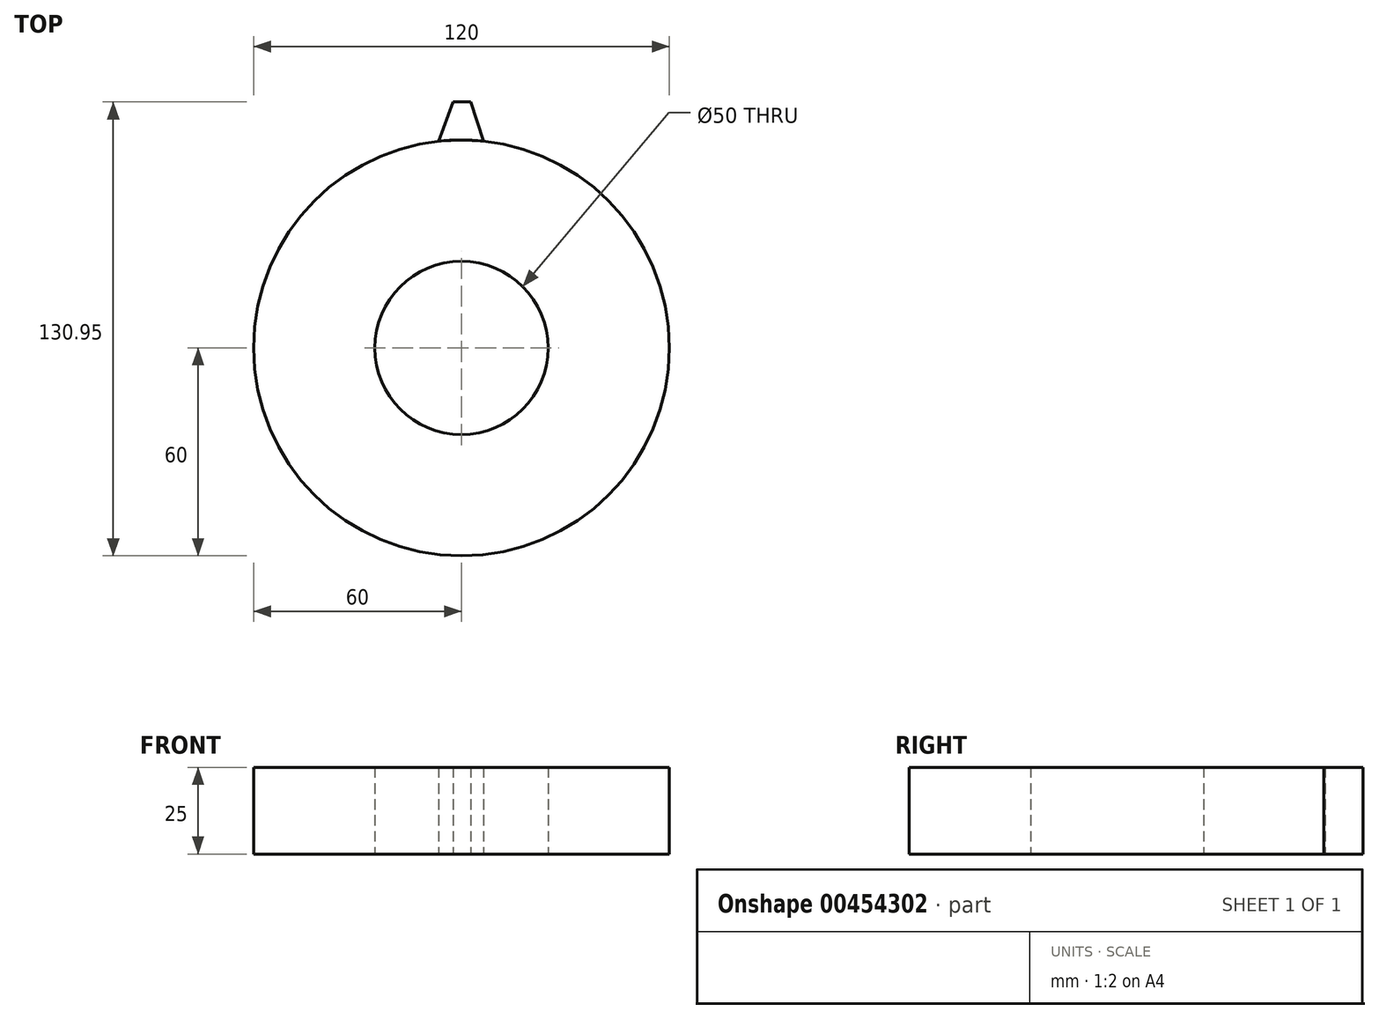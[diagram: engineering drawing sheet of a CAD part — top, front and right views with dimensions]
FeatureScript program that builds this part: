
annotation { "Feature Type Name" : "Feature", "Feature Type Description" : "" }
export const myFeature = defineFeature(function(context is Context, id is Id, definition is map)
    precondition{}
    {
        {
            var Q0;
            Q0=qCreatedBy(makeId("Top.planeOp"),FACE);
            var sketch = newSketch(context, id + "F0", { "sketchPlane" : qUnion([Q0])});
            skCircle(sketch, "E0", {"center": v(0, 0) * mm, "radius": 60 * mm});
            skSolve(sketch);
        }
        {
            var Q0;
            Q0=qCreatedBy(makeId("Top.planeOp"),FACE);
            var sketch = newSketch(context, id + "F1", { "sketchPlane" : qUnion([Q0])});
            skCircle(sketch, "E1", {"center": v(0, 0) * mm, "radius": 25 * mm});
            skSolve(sketch);
        }
        {
            var Q0;
            Q0=qCreatedBy(makeId("Top.planeOp"),FACE);
            var sketch = newSketch(context, id + "F2", { "sketchPlane" : qUnion([Q0])});
            skLineSegment(sketch, "E2", {"start": v(-6.64, 59.63) * mm, "end": v(-2.43, 70.95) * mm});
            skLineSegment(sketch, "E3", {"start": v(-2.43, 70.95) * mm, "end": v(2.67, 70.95) * mm});
            skLineSegment(sketch, "E4", {"start": v(2.67, 70.95) * mm, "end": v(6.3, 59.67) * mm});
            skArc(sketch, "E5", {"start": v(-6.64, 59.63) * mm, "mid": v(-0.17, 60) * mm, "end": v(6.3, 59.67) * mm});
            skSolve(sketch);
        }
        {
            var Q0;
            Q0=qCreatedBy(makeId("Top.planeOp"),FACE);
            var sketch = newSketch(context, id + "F3", { "sketchPlane" : qUnion([Q0])});
            skCircle(sketch, "E6", {"center": v(0, 0) * mm, "radius": 60 * mm});
            skSolve(sketch);
        }
        {
            var Q0;
            Q0 = qSketchRegion(id + "F3", true);
            var Q1;
            Q1 = qSketchRegion(id + "F2", true);
            var Q2;
            Q2=makeQuery(id+"FFwbZkJwYjuvKQh_0.25.F2.imprint","IMPRINT",FACE,{"disambiguationData":[TD([[makeQuery(id+"FFwbZkJwYjuvKQh_0.25.F2.imprint","IMPRINT",EDGE,{"derivedFrom":sQuery(id+"FFwbZkJwYjuvKQh_0.25.F2.wireOp",EDGE,"E2")}),-1.0]])]});
            var Q3;
            Q3=makeQuery(id+"FFwbZkJwYjuvKQh_0.24.F2.imprint","IMPRINT",FACE,{"disambiguationData":[TD([[makeQuery(id+"FFwbZkJwYjuvKQh_0.24.F2.imprint","IMPRINT",EDGE,{"derivedFrom":sQuery(id+"FFwbZkJwYjuvKQh_0.24.F2.wireOp",EDGE,"E2")}),-1.0]])]});
            var Q4;
            Q4=makeQuery(id+"FFwbZkJwYjuvKQh_0.23.F2.imprint","IMPRINT",FACE,{"disambiguationData":[TD([[makeQuery(id+"FFwbZkJwYjuvKQh_0.23.F2.imprint","IMPRINT",EDGE,{"derivedFrom":sQuery(id+"FFwbZkJwYjuvKQh_0.23.F2.wireOp",EDGE,"E2")}),-1.0]])]});
            var Q5;
            Q5=makeQuery(id+"FFwbZkJwYjuvKQh_0.22.F2.imprint","IMPRINT",FACE,{"disambiguationData":[TD([[makeQuery(id+"FFwbZkJwYjuvKQh_0.22.F2.imprint","IMPRINT",EDGE,{"derivedFrom":sQuery(id+"FFwbZkJwYjuvKQh_0.22.F2.wireOp",EDGE,"E2")}),-1.0]])]});
            var Q6;
            Q6=makeQuery(id+"FFwbZkJwYjuvKQh_0.21.F2.imprint","IMPRINT",FACE,{"disambiguationData":[TD([[makeQuery(id+"FFwbZkJwYjuvKQh_0.21.F2.imprint","IMPRINT",EDGE,{"derivedFrom":sQuery(id+"FFwbZkJwYjuvKQh_0.21.F2.wireOp",EDGE,"E2")}),-1.0]])]});
            var Q7;
            Q7=makeQuery(id+"FFwbZkJwYjuvKQh_0.20.F2.imprint","IMPRINT",FACE,{"disambiguationData":[TD([[makeQuery(id+"FFwbZkJwYjuvKQh_0.20.F2.imprint","IMPRINT",EDGE,{"derivedFrom":sQuery(id+"FFwbZkJwYjuvKQh_0.20.F2.wireOp",EDGE,"E2")}),-1.0]])]});
            var Q8;
            Q8=makeQuery(id+"FFwbZkJwYjuvKQh_0.19.F2.imprint","IMPRINT",FACE,{"disambiguationData":[TD([[makeQuery(id+"FFwbZkJwYjuvKQh_0.19.F2.imprint","IMPRINT",EDGE,{"derivedFrom":sQuery(id+"FFwbZkJwYjuvKQh_0.19.F2.wireOp",EDGE,"E2")}),-1.0]])]});
            var Q9;
            Q9=makeQuery(id+"FFwbZkJwYjuvKQh_0.18.F2.imprint","IMPRINT",FACE,{"disambiguationData":[TD([[makeQuery(id+"FFwbZkJwYjuvKQh_0.18.F2.imprint","IMPRINT",EDGE,{"derivedFrom":sQuery(id+"FFwbZkJwYjuvKQh_0.18.F2.wireOp",EDGE,"E2")}),-1.0]])]});
            var Q10;
            Q10=makeQuery(id+"FFwbZkJwYjuvKQh_0.17.F2.imprint","IMPRINT",FACE,{"disambiguationData":[TD([[makeQuery(id+"FFwbZkJwYjuvKQh_0.17.F2.imprint","IMPRINT",EDGE,{"derivedFrom":sQuery(id+"FFwbZkJwYjuvKQh_0.17.F2.wireOp",EDGE,"E2")}),-1.0]])]});
            var Q11;
            Q11=makeQuery(id+"FFwbZkJwYjuvKQh_0.16.F2.imprint","IMPRINT",FACE,{"disambiguationData":[TD([[makeQuery(id+"FFwbZkJwYjuvKQh_0.16.F2.imprint","IMPRINT",EDGE,{"derivedFrom":sQuery(id+"FFwbZkJwYjuvKQh_0.16.F2.wireOp",EDGE,"E2")}),-1.0]])]});
            var Q12;
            Q12=makeQuery(id+"FFwbZkJwYjuvKQh_0.15.F2.imprint","IMPRINT",FACE,{"disambiguationData":[TD([[makeQuery(id+"FFwbZkJwYjuvKQh_0.15.F2.imprint","IMPRINT",EDGE,{"derivedFrom":sQuery(id+"FFwbZkJwYjuvKQh_0.15.F2.wireOp",EDGE,"E2")}),-1.0]])]});
            var Q13;
            Q13=makeQuery(id+"FFwbZkJwYjuvKQh_0.14.F2.imprint","IMPRINT",FACE,{"disambiguationData":[TD([[makeQuery(id+"FFwbZkJwYjuvKQh_0.14.F2.imprint","IMPRINT",EDGE,{"derivedFrom":sQuery(id+"FFwbZkJwYjuvKQh_0.14.F2.wireOp",EDGE,"E2")}),-1.0]])]});
            var Q14;
            Q14=makeQuery(id+"FFwbZkJwYjuvKQh_0.13.F2.imprint","IMPRINT",FACE,{"disambiguationData":[TD([[makeQuery(id+"FFwbZkJwYjuvKQh_0.13.F2.imprint","IMPRINT",EDGE,{"derivedFrom":sQuery(id+"FFwbZkJwYjuvKQh_0.13.F2.wireOp",EDGE,"E2")}),-1.0]])]});
            var Q15;
            Q15=makeQuery(id+"FFwbZkJwYjuvKQh_0.12.F2.imprint","IMPRINT",FACE,{"disambiguationData":[TD([[makeQuery(id+"FFwbZkJwYjuvKQh_0.12.F2.imprint","IMPRINT",EDGE,{"derivedFrom":sQuery(id+"FFwbZkJwYjuvKQh_0.12.F2.wireOp",EDGE,"E2")}),-1.0]])]});
            var Q16;
            Q16=makeQuery(id+"FFwbZkJwYjuvKQh_0.11.F2.imprint","IMPRINT",FACE,{"disambiguationData":[TD([[makeQuery(id+"FFwbZkJwYjuvKQh_0.11.F2.imprint","IMPRINT",EDGE,{"derivedFrom":sQuery(id+"FFwbZkJwYjuvKQh_0.11.F2.wireOp",EDGE,"E2")}),-1.0]])]});
            var Q17;
            Q17=makeQuery(id+"FFwbZkJwYjuvKQh_0.10.F2.imprint","IMPRINT",FACE,{"disambiguationData":[TD([[makeQuery(id+"FFwbZkJwYjuvKQh_0.10.F2.imprint","IMPRINT",EDGE,{"derivedFrom":sQuery(id+"FFwbZkJwYjuvKQh_0.10.F2.wireOp",EDGE,"E2")}),-1.0]])]});
            var Q18;
            Q18=makeQuery(id+"FFwbZkJwYjuvKQh_0.9.F2.imprint","IMPRINT",FACE,{"disambiguationData":[TD([[makeQuery(id+"FFwbZkJwYjuvKQh_0.9.F2.imprint","IMPRINT",EDGE,{"derivedFrom":sQuery(id+"FFwbZkJwYjuvKQh_0.9.F2.wireOp",EDGE,"E2")}),-1.0]])]});
            var Q19;
            Q19=makeQuery(id+"FFwbZkJwYjuvKQh_0.8.F2.imprint","IMPRINT",FACE,{"disambiguationData":[TD([[makeQuery(id+"FFwbZkJwYjuvKQh_0.8.F2.imprint","IMPRINT",EDGE,{"derivedFrom":sQuery(id+"FFwbZkJwYjuvKQh_0.8.F2.wireOp",EDGE,"E2")}),-1.0]])]});
            var Q20;
            Q20=makeQuery(id+"FFwbZkJwYjuvKQh_0.7.F2.imprint","IMPRINT",FACE,{"disambiguationData":[TD([[makeQuery(id+"FFwbZkJwYjuvKQh_0.7.F2.imprint","IMPRINT",EDGE,{"derivedFrom":sQuery(id+"FFwbZkJwYjuvKQh_0.7.F2.wireOp",EDGE,"E2")}),-1.0]])]});
            var Q21;
            Q21=makeQuery(id+"FFwbZkJwYjuvKQh_0.6.F2.imprint","IMPRINT",FACE,{"disambiguationData":[TD([[makeQuery(id+"FFwbZkJwYjuvKQh_0.6.F2.imprint","IMPRINT",EDGE,{"derivedFrom":sQuery(id+"FFwbZkJwYjuvKQh_0.6.F2.wireOp",EDGE,"E2")}),-1.0]])]});
            var Q22;
            Q22=makeQuery(id+"FFwbZkJwYjuvKQh_0.5.F2.imprint","IMPRINT",FACE,{"disambiguationData":[TD([[makeQuery(id+"FFwbZkJwYjuvKQh_0.5.F2.imprint","IMPRINT",EDGE,{"derivedFrom":sQuery(id+"FFwbZkJwYjuvKQh_0.5.F2.wireOp",EDGE,"E2")}),-1.0]])]});
            var Q23;
            Q23=makeQuery(id+"FFwbZkJwYjuvKQh_0.4.F2.imprint","IMPRINT",FACE,{"disambiguationData":[TD([[makeQuery(id+"FFwbZkJwYjuvKQh_0.4.F2.imprint","IMPRINT",EDGE,{"derivedFrom":sQuery(id+"FFwbZkJwYjuvKQh_0.4.F2.wireOp",EDGE,"E2")}),-1.0]])]});
            var Q24;
            Q24=makeQuery(id+"FFwbZkJwYjuvKQh_0.3.F2.imprint","IMPRINT",FACE,{"disambiguationData":[TD([[makeQuery(id+"FFwbZkJwYjuvKQh_0.3.F2.imprint","IMPRINT",EDGE,{"derivedFrom":sQuery(id+"FFwbZkJwYjuvKQh_0.3.F2.wireOp",EDGE,"E2")}),-1.0]])]});
            var Q25;
            Q25=makeQuery(id+"FFwbZkJwYjuvKQh_0.2.F2.imprint","IMPRINT",FACE,{"disambiguationData":[TD([[makeQuery(id+"FFwbZkJwYjuvKQh_0.2.F2.imprint","IMPRINT",EDGE,{"derivedFrom":sQuery(id+"FFwbZkJwYjuvKQh_0.2.F2.wireOp",EDGE,"E2")}),-1.0]])]});
            var Q26;
            Q26=makeQuery(id+"FFwbZkJwYjuvKQh_0.1.F2.imprint","IMPRINT",FACE,{"disambiguationData":[TD([[makeQuery(id+"FFwbZkJwYjuvKQh_0.1.F2.imprint","IMPRINT",EDGE,{"derivedFrom":sQuery(id+"FFwbZkJwYjuvKQh_0.1.F2.wireOp",EDGE,"E2")}),-1.0]])]});
            extrude(context, id + "F4", {"entities" : qUnion([Q0, Q1, Q2, Q3, Q4, Q5, Q6, Q7, Q8, Q9, Q10, Q11, Q12, Q13, Q14, Q15, Q16, Q17, Q18, Q19, Q20, Q21, Q22, Q23, Q24, Q25, Q26]), "depth" : 25 * mm});
        }
        {
            var Q0;
            Q0=makeQuery(id+"F1.imprint","IMPRINT",FACE,{"disambiguationData":[TD([[makeQuery(id+"F1.imprint","IMPRINT",EDGE,{"derivedFrom":sQuery(id+"F1.wireOp",EDGE,"E1")}),1.0]])]});
            extrude(context, id + "F5", {"entities" : qUnion([Q0]), "operationType" : NewBodyOperationType.REMOVE, "oppositeDirection" : true, "depth" : -25 * mm});
        }
    });
